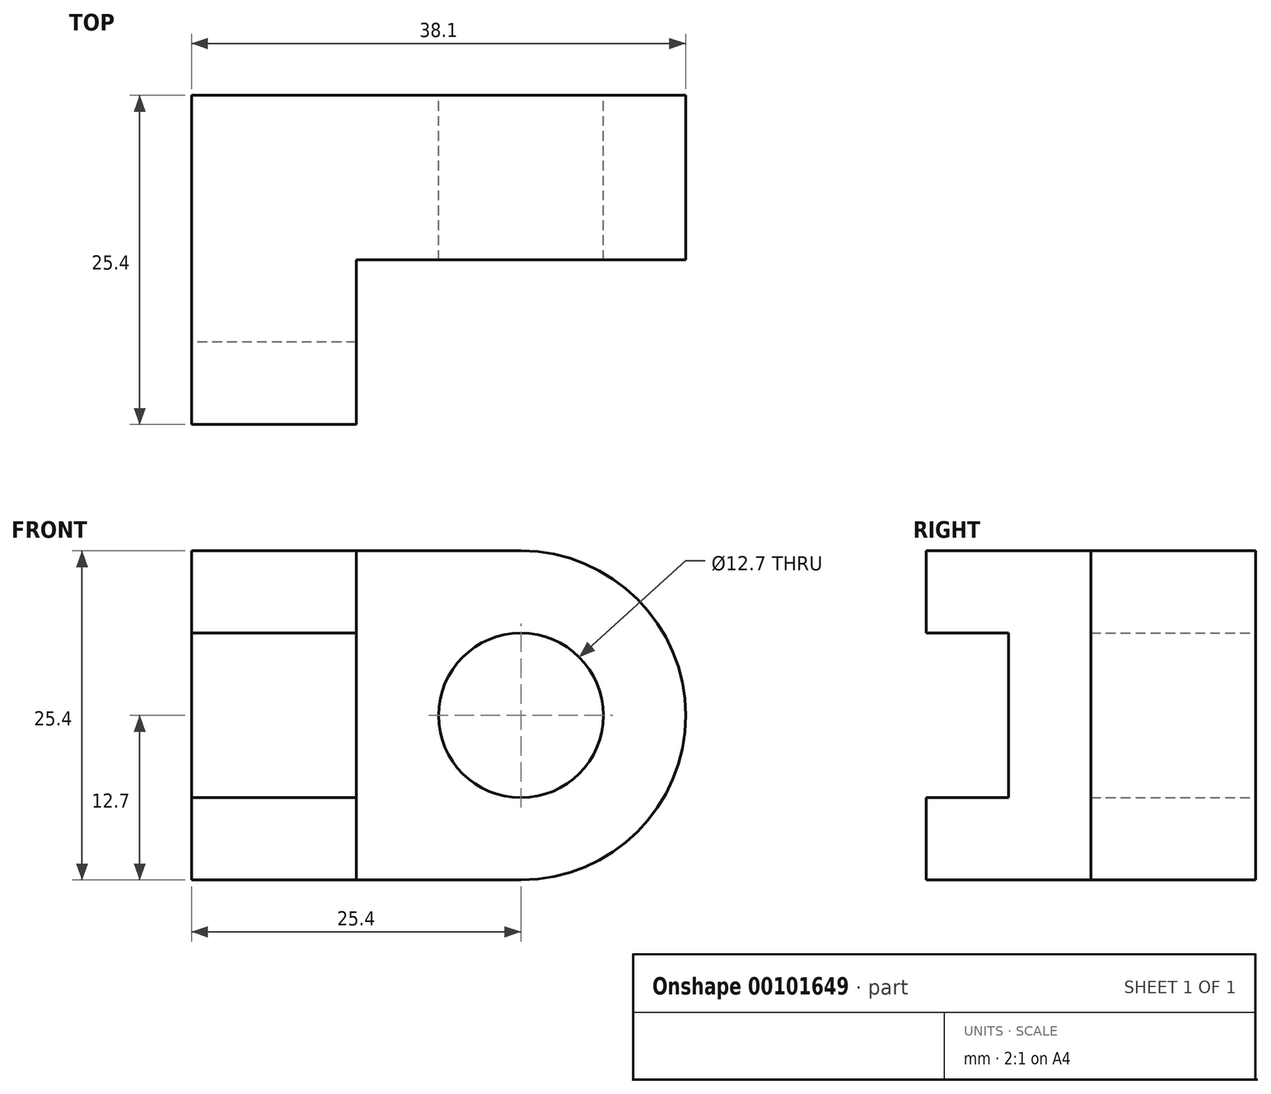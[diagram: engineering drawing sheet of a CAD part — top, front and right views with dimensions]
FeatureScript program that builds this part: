
annotation { "Feature Type Name" : "Feature", "Feature Type Description" : "" }
export const myFeature = defineFeature(function(context is Context, id is Id, definition is map)
    precondition{}
    {
        {
            var Q0;
            Q0=qCreatedBy(makeId("Front.planeOp"),FACE);
            var sketch = newSketch(context, id + "F0", { "sketchPlane" : qUnion([Q0])});
            skLineSegment(sketch, "E0", {"start": v(0, 0) * mm, "end": v(25.4, 0) * mm});
            skLineSegment(sketch, "E1", {"start": v(0, 0) * mm, "end": v(0, 25.4) * mm});
            skLineSegment(sketch, "E2", {"start": v(0, 25.4) * mm, "end": v(25.4, 25.4) * mm});
            skCircle(sketch, "E3", {"center": v(25.4, 12.7) * mm, "radius": 6.35 * mm});
            skArc(sketch, "E4", {"start": v(25.4, 25.4) * mm, "mid": v(38.1, 12.7) * mm, "end": v(25.4, 0) * mm});
            skSolve(sketch);
        }
        {
            var Q0;
            Q0=qCreatedBy(makeId("Right.planeOp"),FACE);
            var sketch = newSketch(context, id + "F1", { "sketchPlane" : qUnion([Q0])});
            skLineSegment(sketch, "E5", {"start": v(0, 0) * mm, "end": v(0, 25.4) * mm});
            skLineSegment(sketch, "E6", {"start": v(0, 25.4) * mm, "end": v(-25.4, 25.4) * mm});
            skLineSegment(sketch, "E7", {"start": v(-25.4, 25.4) * mm, "end": v(-25.4, 19.05) * mm});
            skLineSegment(sketch, "E8", {"start": v(-25.4, 19.05) * mm, "end": v(-19.05, 19.05) * mm});
            skLineSegment(sketch, "E9", {"start": v(-19.05, 19.05) * mm, "end": v(-19.05, 6.35) * mm});
            skLineSegment(sketch, "E10", {"start": v(-19.05, 6.35) * mm, "end": v(-25.4, 6.35) * mm});
            skLineSegment(sketch, "E11", {"start": v(-25.4, 6.35) * mm, "end": v(-25.4, 0) * mm});
            skLineSegment(sketch, "E12", {"start": v(-25.4, 0) * mm, "end": v(0, 0) * mm});
            skSolve(sketch);
        }
        {
            var Q0;
            Q0=makeQuery(id+"F1.imprint","IMPRINT",FACE,{"disambiguationData":[TD([[makeQuery(id+"F1.imprint","IMPRINT",EDGE,{"derivedFrom":sQuery(id+"F1.wireOp",EDGE,"E5")}),1.0]])]});
            extrude(context, id + "F2", {"entities" : qUnion([Q0]), "depth" : 12.7 * mm});
        }
        {
            var Q0;
            Q0=makeQuery(id+"F0.imprint","IMPRINT",FACE,{"disambiguationData":[TD([[makeQuery(id+"F0.imprint","IMPRINT",EDGE,{"derivedFrom":sQuery(id+"F0.wireOp",EDGE,"E0")}),1.0]])]});
            extrude(context, id + "F3", {"entities" : qUnion([Q0]), "operationType" : NewBodyOperationType.ADD, "depth" : 12.7 * mm});
        }
    });
